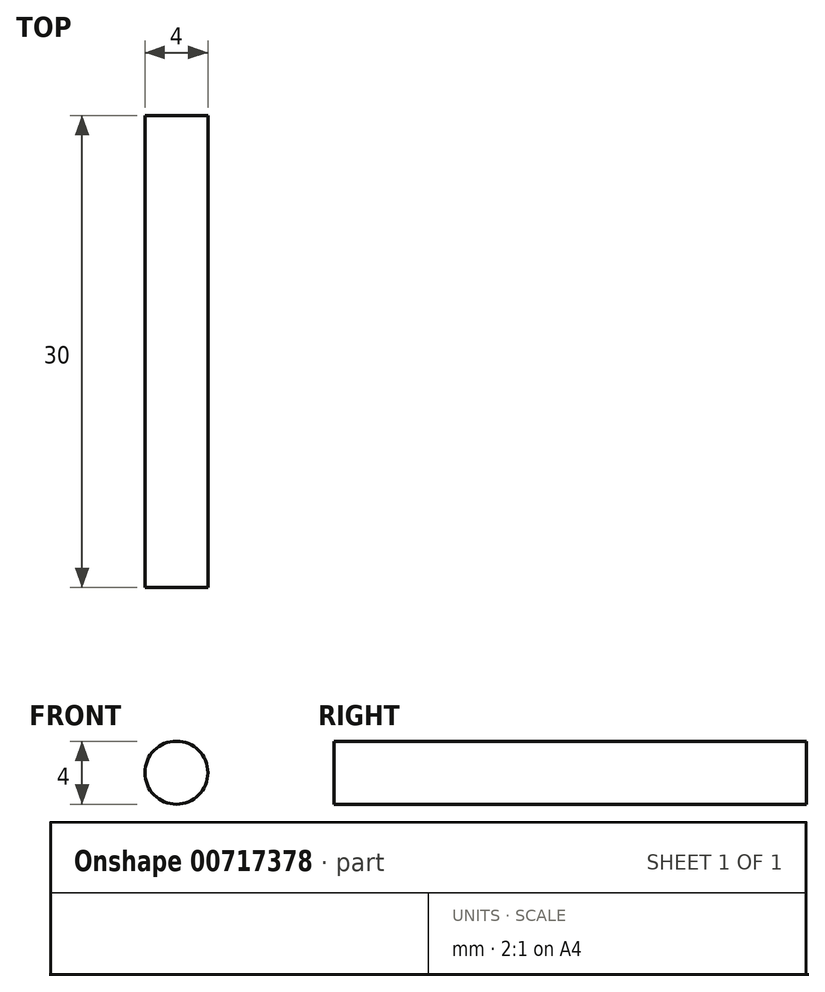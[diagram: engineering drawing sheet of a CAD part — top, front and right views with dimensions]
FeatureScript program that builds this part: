
annotation { "Feature Type Name" : "Feature", "Feature Type Description" : "" }
export const myFeature = defineFeature(function(context is Context, id is Id, definition is map)
    precondition{}
    {
        {
            var Q0;
            Q0=qCreatedBy(makeId("Front.planeOp"),FACE);
            var sketch = newSketch(context, id + "F0", { "sketchPlane" : qUnion([Q0])});
            skCircle(sketch, "E0", {"center": v(0, 0) * mm, "radius": 2 * mm});
            skSolve(sketch);
        }
        {
            var Q0;
            Q0=makeQuery(id+"F0.imprint","IMPRINT",FACE,{"disambiguationData":[TD([[makeQuery(id+"F0.imprint","IMPRINT",EDGE,{"derivedFrom":sQuery(id+"F0.wireOp",EDGE,"E0")}),1.0]])]});
            extrude(context, id + "F1", {"entities" : qUnion([Q0]), "depth" : 30 * mm, "offsetDistance" : 25 * mm});
        }
    });
